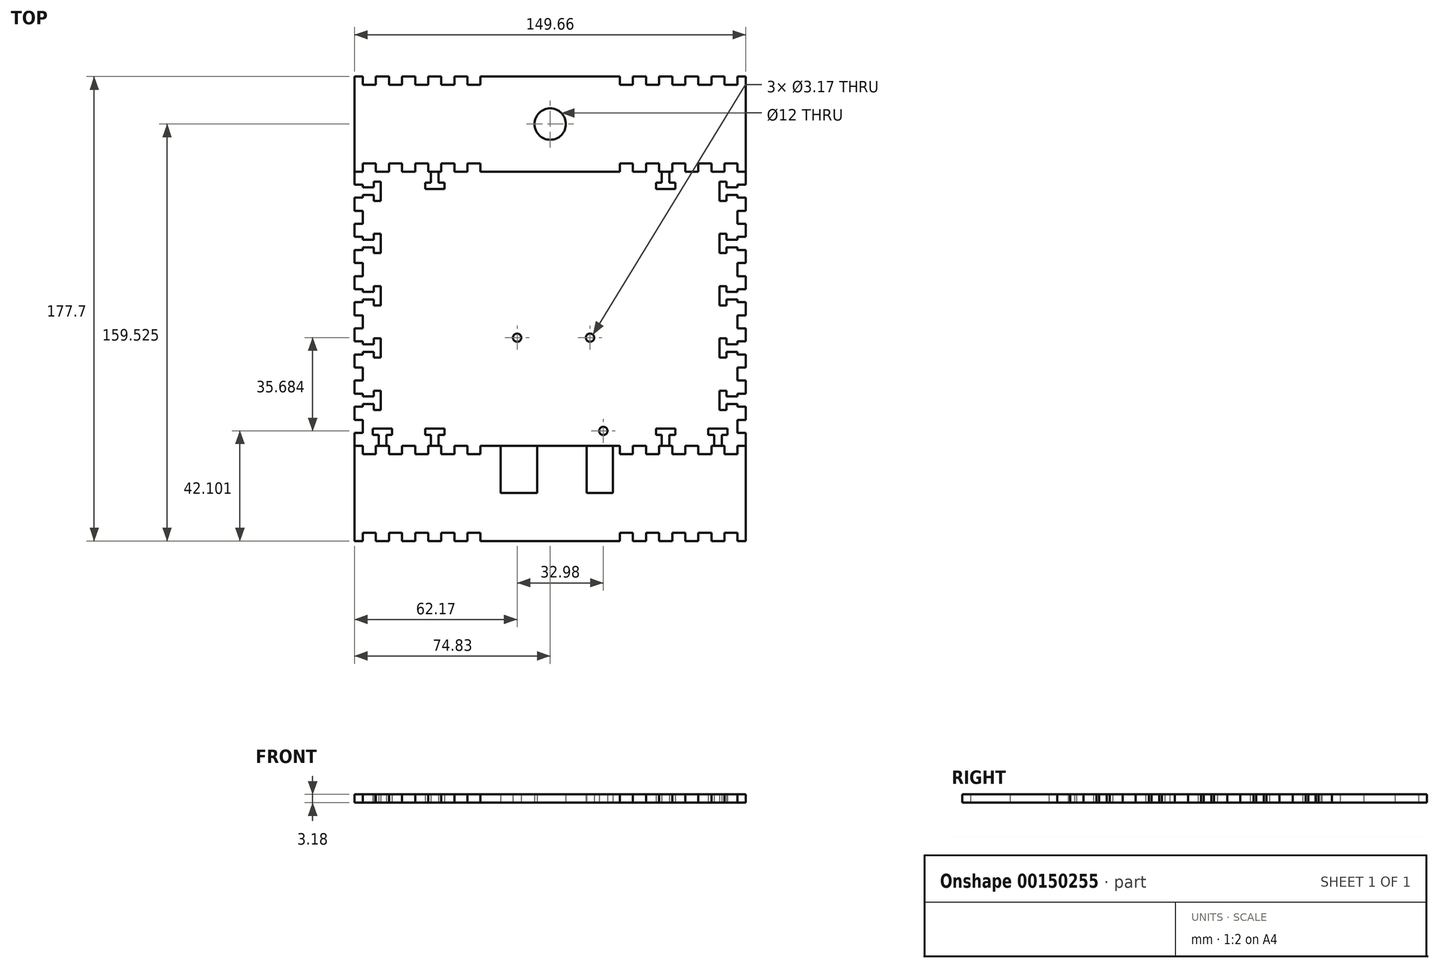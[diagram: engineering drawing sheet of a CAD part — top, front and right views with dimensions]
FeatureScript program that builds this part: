
annotation { "Feature Type Name" : "Feature", "Feature Type Description" : "" }
export const myFeature = defineFeature(function(context is Context, id is Id, definition is map)
    precondition{}
    {
        {
            var Q0;
            Q0=qCreatedBy(makeId("Top.planeOp"),FACE);
            var sketch = newSketch(context, id + "F0", { "sketchPlane" : qUnion([Q0])});
            skLineSegment(sketch, "E0", {"start": v(0, 0) * mm, "end": v(26.65, 0) * mm});
            skLineSegment(sketch, "E1", {"start": v(31.65, 0) * mm, "end": v(36.65, 0) * mm});
            skLineSegment(sketch, "E2", {"start": v(71.65, 5) * mm, "end": v(71.65, 10) * mm});
            skLineSegment(sketch, "E3", {"start": v(66.65, 105) * mm, "end": v(61.65, 105) * mm});
            skLineSegment(sketch, "E4.bottom", {"start": v(0, 105) * mm, "end": v(14.7, 105) * mm});
            skLineSegment(sketch, "E5", {"start": v(71.65, 0) * mm, "end": v(71.65, -3.17) * mm});
            skLineSegment(sketch, "E6", {"start": v(71.65, -3.17) * mm, "end": v(66.65, -3.17) * mm});
            skLineSegment(sketch, "E7", {"start": v(66.65, -3.17) * mm, "end": v(66.65, 0) * mm});
            skLineSegment(sketch, "E8.1.0.0", {"start": v(61.65, 0) * mm, "end": v(61.65, -3.17) * mm});
            skLineSegment(sketch, "E8.1.0.1", {"start": v(61.65, -3.17) * mm, "end": v(56.65, -3.17) * mm});
            skLineSegment(sketch, "E8.1.0.2", {"start": v(56.65, -3.17) * mm, "end": v(56.65, 0) * mm});
            skLineSegment(sketch, "E8.2.0.0", {"start": v(51.65, 0) * mm, "end": v(51.65, -3.17) * mm});
            skLineSegment(sketch, "E8.2.0.1", {"start": v(51.65, -3.17) * mm, "end": v(46.65, -3.17) * mm});
            skLineSegment(sketch, "E8.2.0.2", {"start": v(46.65, -3.17) * mm, "end": v(46.65, 0) * mm});
            skLineSegment(sketch, "E8.3.0.0", {"start": v(41.65, 0) * mm, "end": v(41.65, -3.17) * mm});
            skLineSegment(sketch, "E8.3.0.1", {"start": v(41.65, -3.17) * mm, "end": v(36.65, -3.17) * mm});
            skLineSegment(sketch, "E8.3.0.2", {"start": v(36.65, -3.17) * mm, "end": v(36.65, 0) * mm});
            skLineSegment(sketch, "E8.4.0.0", {"start": v(31.65, 0) * mm, "end": v(31.65, -3.17) * mm});
            skLineSegment(sketch, "E8.4.0.1", {"start": v(31.65, -3.17) * mm, "end": v(26.65, -3.17) * mm});
            skLineSegment(sketch, "E8.4.0.2", {"start": v(26.65, -3.17) * mm, "end": v(26.65, 0) * mm});
            skLineSegment(sketch, "E9", {"start": v(71.65, 0) * mm, "end": v(74.83, 0) * mm});
            skLineSegment(sketch, "E10", {"start": v(74.83, 0) * mm, "end": v(74.83, 5) * mm});
            skLineSegment(sketch, "E11", {"start": v(74.83, 5) * mm, "end": v(71.65, 5) * mm});
            skLineSegment(sketch, "E12.0.1.0", {"start": v(71.65, 10) * mm, "end": v(74.83, 10) * mm});
            skLineSegment(sketch, "E12.0.1.1", {"start": v(74.83, 10) * mm, "end": v(74.83, 15) * mm});
            skLineSegment(sketch, "E12.0.1.2", {"start": v(74.83, 15) * mm, "end": v(71.65, 15) * mm});
            skLineSegment(sketch, "E12.0.2.0", {"start": v(71.65, 20) * mm, "end": v(74.83, 20) * mm});
            skLineSegment(sketch, "E12.0.2.1", {"start": v(74.83, 20) * mm, "end": v(74.83, 25) * mm});
            skLineSegment(sketch, "E12.0.2.2", {"start": v(74.83, 25) * mm, "end": v(71.65, 25) * mm});
            skLineSegment(sketch, "E12.0.3.0", {"start": v(71.65, 30) * mm, "end": v(74.83, 30) * mm});
            skLineSegment(sketch, "E12.0.3.1", {"start": v(74.83, 30) * mm, "end": v(74.83, 35) * mm});
            skLineSegment(sketch, "E12.0.3.2", {"start": v(74.83, 35) * mm, "end": v(71.65, 35) * mm});
            skLineSegment(sketch, "E12.0.4.0", {"start": v(71.65, 40) * mm, "end": v(74.83, 40) * mm});
            skLineSegment(sketch, "E12.0.4.1", {"start": v(74.83, 40) * mm, "end": v(74.83, 45) * mm});
            skLineSegment(sketch, "E12.0.4.2", {"start": v(74.83, 45) * mm, "end": v(71.65, 45) * mm});
            skLineSegment(sketch, "E12.0.5.0", {"start": v(71.65, 50) * mm, "end": v(74.83, 50) * mm});
            skLineSegment(sketch, "E12.0.5.1", {"start": v(74.83, 50) * mm, "end": v(74.83, 55) * mm});
            skLineSegment(sketch, "E12.0.5.2", {"start": v(74.83, 55) * mm, "end": v(71.65, 55) * mm});
            skLineSegment(sketch, "E12.0.6.0", {"start": v(71.65, 60) * mm, "end": v(74.83, 60) * mm});
            skLineSegment(sketch, "E12.0.6.1", {"start": v(74.83, 60) * mm, "end": v(74.83, 65) * mm});
            skLineSegment(sketch, "E12.0.6.2", {"start": v(74.83, 65) * mm, "end": v(71.65, 65) * mm});
            skLineSegment(sketch, "E12.0.7.0", {"start": v(71.65, 70) * mm, "end": v(74.83, 70) * mm});
            skLineSegment(sketch, "E12.0.7.1", {"start": v(74.83, 70) * mm, "end": v(74.83, 75) * mm});
            skLineSegment(sketch, "E12.0.7.2", {"start": v(74.83, 75) * mm, "end": v(71.65, 75) * mm});
            skLineSegment(sketch, "E12.0.8.0", {"start": v(71.65, 80) * mm, "end": v(74.83, 80) * mm});
            skLineSegment(sketch, "E12.0.8.1", {"start": v(74.83, 80) * mm, "end": v(74.83, 85) * mm});
            skLineSegment(sketch, "E12.0.8.2", {"start": v(74.83, 85) * mm, "end": v(71.65, 85) * mm});
            skLineSegment(sketch, "E12.0.9.0", {"start": v(71.65, 90) * mm, "end": v(74.83, 90) * mm});
            skLineSegment(sketch, "E12.0.9.1", {"start": v(74.83, 90) * mm, "end": v(74.83, 95) * mm});
            skLineSegment(sketch, "E12.0.9.2", {"start": v(74.83, 95) * mm, "end": v(71.65, 95) * mm});
            skLineSegment(sketch, "E12.0.10.0", {"start": v(71.65, 100) * mm, "end": v(74.83, 100) * mm});
            skLineSegment(sketch, "E12.0.10.1", {"start": v(74.83, 100) * mm, "end": v(74.83, 105) * mm});
            skLineSegment(sketch, "E12.0.10.2", {"start": v(74.83, 105) * mm, "end": v(71.65, 105) * mm});
            skLineSegment(sketch, "E12.direction2", {"start": v(71.65, 5) * mm, "end": v(71.65, 10) * mm, "construction": true});
            skLineSegment(sketch, "E13.MirrorCS", {"start": v(26.65, 108.18) * mm, "end": v(26.65, 105) * mm});
            skLineSegment(sketch, "E14.MirrorCS", {"start": v(31.65, 108.17) * mm, "end": v(26.65, 108.17) * mm});
            skLineSegment(sketch, "E15.MirrorCS", {"start": v(31.65, 105) * mm, "end": v(31.65, 108.17) * mm});
            skLineSegment(sketch, "E16.MirrorCS", {"start": v(36.65, 108.18) * mm, "end": v(36.65, 105) * mm});
            skLineSegment(sketch, "E17.MirrorCS", {"start": v(41.65, 108.17) * mm, "end": v(36.65, 108.17) * mm});
            skLineSegment(sketch, "E18.MirrorCS", {"start": v(41.65, 105) * mm, "end": v(41.65, 108.17) * mm});
            skLineSegment(sketch, "E19.MirrorCS", {"start": v(61.65, 105) * mm, "end": v(61.65, 108.17) * mm});
            skLineSegment(sketch, "E20.MirrorCS", {"start": v(61.65, 108.17) * mm, "end": v(56.65, 108.17) * mm});
            skLineSegment(sketch, "E21.MirrorCS", {"start": v(56.65, 108.18) * mm, "end": v(56.65, 105) * mm});
            skLineSegment(sketch, "E22.MirrorCS", {"start": v(66.65, 108.18) * mm, "end": v(66.65, 105) * mm});
            skLineSegment(sketch, "E23.MirrorCS", {"start": v(71.65, 105) * mm, "end": v(71.65, 108.17) * mm});
            skLineSegment(sketch, "E24.MirrorCS", {"start": v(71.65, 108.17) * mm, "end": v(61.65, 108.17) * mm, "construction": true});
            skLineSegment(sketch, "E25.MirrorCS", {"start": v(46.65, 108.18) * mm, "end": v(46.65, 105) * mm});
            skLineSegment(sketch, "E26.MirrorCS", {"start": v(51.65, 108.17) * mm, "end": v(46.65, 108.17) * mm});
            skLineSegment(sketch, "E27.MirrorCS", {"start": v(51.65, 105) * mm, "end": v(51.65, 108.17) * mm});
            skLineSegment(sketch, "E28.MirrorCS", {"start": v(71.65, 108.17) * mm, "end": v(66.65, 108.17) * mm});
            skLineSegment(sketch, "E29.MirrorCS", {"start": v(-71.65, 105) * mm, "end": v(-71.65, 108.17) * mm});
            skLineSegment(sketch, "E30.MirrorCS", {"start": v(-31.65, 108.17) * mm, "end": v(-26.65, 108.17) * mm});
            skLineSegment(sketch, "E31.MirrorCS", {"start": v(-71.65, 108.17) * mm, "end": v(-61.65, 108.17) * mm, "construction": true});
            skLineSegment(sketch, "E32.MirrorCS", {"start": v(-26.65, 108.18) * mm, "end": v(-26.65, 105) * mm});
            skLineSegment(sketch, "E33.MirrorCS", {"start": v(-41.65, 105) * mm, "end": v(-41.65, 108.17) * mm});
            skLineSegment(sketch, "E34.MirrorCS", {"start": v(-71.65, 0) * mm, "end": v(-71.65, -3.18) * mm});
            skLineSegment(sketch, "E35.MirrorCS", {"start": v(-46.65, 108.18) * mm, "end": v(-46.65, 105) * mm});
            skLineSegment(sketch, "E36.MirrorCS", {"start": v(-36.65, 108.18) * mm, "end": v(-36.65, 105) * mm});
            skLineSegment(sketch, "E37.MirrorCS", {"start": v(-66.65, 108.17) * mm, "end": v(-66.65, 105) * mm});
            skLineSegment(sketch, "E38.MirrorCS", {"start": v(-31.65, 105) * mm, "end": v(-31.65, 108.17) * mm});
            skLineSegment(sketch, "E39.MirrorCS", {"start": v(-71.65, 108.17) * mm, "end": v(-66.65, 108.17) * mm});
            skLineSegment(sketch, "E40.MirrorCS", {"start": v(-56.65, 108.17) * mm, "end": v(-56.65, 105) * mm});
            skLineSegment(sketch, "E41.MirrorCS", {"start": v(-51.65, 105) * mm, "end": v(-51.65, 108.17) * mm});
            skLineSegment(sketch, "E42.MirrorCS", {"start": v(-61.65, 105) * mm, "end": v(-61.65, 108.17) * mm});
            skLineSegment(sketch, "E43.MirrorCS", {"start": v(-71.65, -3.18) * mm, "end": v(-66.65, -3.18) * mm});
            skLineSegment(sketch, "E44.MirrorCS", {"start": v(-74.83, 0) * mm, "end": v(-74.83, 5) * mm});
            skLineSegment(sketch, "E45.MirrorCS", {"start": v(-66.65, -3.18) * mm, "end": v(-66.65, 0) * mm});
            skLineSegment(sketch, "E46.MirrorCS", {"start": v(-74.83, 80) * mm, "end": v(-74.83, 85) * mm});
            skLineSegment(sketch, "E47.MirrorCS", {"start": v(-74.83, 105) * mm, "end": v(-71.65, 105) * mm});
            skLineSegment(sketch, "E48.MirrorCS", {"start": v(-71.65, 0) * mm, "end": v(-74.83, 0) * mm});
            skLineSegment(sketch, "E49.MirrorCS", {"start": v(-71.65, -3.18) * mm, "end": v(-61.65, -3.18) * mm, "construction": true});
            skLineSegment(sketch, "E50.MirrorCS", {"start": v(-74.83, 90) * mm, "end": v(-74.83, 95) * mm});
            skLineSegment(sketch, "E51.MirrorCS", {"start": v(-74.83, 70) * mm, "end": v(-74.83, 75) * mm});
            skLineSegment(sketch, "E52.MirrorCS", {"start": v(-74.83, 10) * mm, "end": v(-74.83, 15) * mm});
            skLineSegment(sketch, "E53.MirrorCS", {"start": v(-26.65, -3.18) * mm, "end": v(-26.65, 0) * mm});
            skLineSegment(sketch, "E54.MirrorCS", {"start": v(-71.65, 10) * mm, "end": v(-74.83, 10) * mm});
            skLineSegment(sketch, "E55.MirrorCS", {"start": v(-74.83, 60) * mm, "end": v(-74.83, 65) * mm});
            skLineSegment(sketch, "E56.MirrorCS", {"start": v(-74.83, 20) * mm, "end": v(-74.83, 25) * mm});
            skLineSegment(sketch, "E57.MirrorCS", {"start": v(-31.65, -3.18) * mm, "end": v(-26.65, -3.18) * mm});
            skLineSegment(sketch, "E58.MirrorCS", {"start": v(-74.83, 85) * mm, "end": v(-71.65, 85) * mm});
            skLineSegment(sketch, "E59.MirrorCS", {"start": v(-74.83, 55) * mm, "end": v(-71.65, 55) * mm});
            skLineSegment(sketch, "E60.MirrorCS", {"start": v(-71.65, 60) * mm, "end": v(-74.83, 60) * mm});
            skLineSegment(sketch, "E61.MirrorCS", {"start": v(-74.83, 5) * mm, "end": v(-71.65, 5) * mm});
            skLineSegment(sketch, "E62.MirrorCS", {"start": v(-41.65, 0) * mm, "end": v(-41.65, -3.18) * mm});
            skLineSegment(sketch, "E63.MirrorCS", {"start": v(-71.65, 30) * mm, "end": v(-74.83, 30) * mm});
            skLineSegment(sketch, "E64.MirrorCS", {"start": v(-51.65, 108.17) * mm, "end": v(-46.65, 108.17) * mm});
            skLineSegment(sketch, "E65.MirrorCS", {"start": v(-61.65, 108.17) * mm, "end": v(-56.65, 108.17) * mm});
            skLineSegment(sketch, "E66.MirrorCS", {"start": v(-71.65, 90) * mm, "end": v(-74.83, 90) * mm});
            skLineSegment(sketch, "E67.MirrorCS", {"start": v(-74.83, 35) * mm, "end": v(-71.65, 35) * mm});
            skLineSegment(sketch, "E68.MirrorCS", {"start": v(-36.65, -3.18) * mm, "end": v(-36.65, 0) * mm});
            skLineSegment(sketch, "E69.MirrorCS", {"start": v(-46.65, -3.18) * mm, "end": v(-46.65, 0) * mm});
            skLineSegment(sketch, "E70.MirrorCS", {"start": v(-74.83, 25) * mm, "end": v(-71.65, 25) * mm});
            skLineSegment(sketch, "E71.MirrorCS", {"start": v(-71.65, 80) * mm, "end": v(-74.83, 80) * mm});
            skLineSegment(sketch, "E72.MirrorCS", {"start": v(-71.65, 50) * mm, "end": v(-74.83, 50) * mm});
            skLineSegment(sketch, "E73.MirrorCS", {"start": v(-74.83, 45) * mm, "end": v(-71.65, 45) * mm});
            skLineSegment(sketch, "E74.MirrorCS", {"start": v(-51.65, -3.18) * mm, "end": v(-46.65, -3.18) * mm});
            skLineSegment(sketch, "E75.MirrorCS", {"start": v(-56.65, 0) * mm, "end": v(-51.65, 0) * mm});
            skLineSegment(sketch, "E76.MirrorCS", {"start": v(-74.83, 75) * mm, "end": v(-71.65, 75) * mm});
            skLineSegment(sketch, "E77.MirrorCS", {"start": v(-71.65, 100) * mm, "end": v(-74.83, 100) * mm});
            skLineSegment(sketch, "E78.MirrorCS", {"start": v(-31.65, 0) * mm, "end": v(-31.65, -3.18) * mm});
            skLineSegment(sketch, "E79.MirrorCS", {"start": v(-74.83, 15) * mm, "end": v(-71.65, 15) * mm});
            skLineSegment(sketch, "E80.MirrorCS", {"start": v(-56.65, -3.18) * mm, "end": v(-56.65, 0) * mm});
            skLineSegment(sketch, "E81.MirrorCS", {"start": v(-71.65, 40) * mm, "end": v(-74.83, 40) * mm});
            skLineSegment(sketch, "E82.MirrorCS", {"start": v(-71.65, 70) * mm, "end": v(-74.83, 70) * mm});
            skLineSegment(sketch, "E83.MirrorCS", {"start": v(-74.83, 95) * mm, "end": v(-71.65, 95) * mm});
            skLineSegment(sketch, "E84.MirrorCS", {"start": v(-61.65, -3.18) * mm, "end": v(-56.65, -3.18) * mm});
            skLineSegment(sketch, "E85.MirrorCS", {"start": v(-74.83, 65) * mm, "end": v(-71.65, 65) * mm});
            skLineSegment(sketch, "E86.MirrorCS", {"start": v(-61.65, 0) * mm, "end": v(-61.65, -3.18) * mm});
            skLineSegment(sketch, "E87.MirrorCS", {"start": v(-41.65, 108.17) * mm, "end": v(-36.65, 108.17) * mm});
            skLineSegment(sketch, "E88.MirrorCS", {"start": v(-51.65, 0) * mm, "end": v(-51.65, -3.18) * mm});
            skLineSegment(sketch, "E89.MirrorCS", {"start": v(-71.65, 20) * mm, "end": v(-74.83, 20) * mm});
            skLineSegment(sketch, "E90.MirrorCS", {"start": v(-41.65, -3.18) * mm, "end": v(-36.65, -3.18) * mm});
            skLineSegment(sketch, "E91.MirrorCS", {"start": v(-74.83, 30) * mm, "end": v(-74.83, 35) * mm});
            skLineSegment(sketch, "E92.MirrorCS", {"start": v(-71.65, 5) * mm, "end": v(-71.65, 10) * mm, "construction": true});
            skLineSegment(sketch, "E93.MirrorCS", {"start": v(-74.83, 50) * mm, "end": v(-74.83, 55) * mm});
            skLineSegment(sketch, "E94.MirrorCS", {"start": v(-74.83, 100) * mm, "end": v(-74.83, 105) * mm});
            skLineSegment(sketch, "E95.MirrorCS", {"start": v(0, 105) * mm, "end": v(-14.7, 105) * mm});
            skLineSegment(sketch, "E96.MirrorCS", {"start": v(-71.65, 5) * mm, "end": v(-71.65, 10) * mm});
            skLineSegment(sketch, "E97.MirrorCS", {"start": v(-31.65, 0) * mm, "end": v(-36.65, 0) * mm});
            skLineSegment(sketch, "E98.MirrorCS", {"start": v(-74.83, 40) * mm, "end": v(-74.83, 45) * mm});
            skLineSegment(sketch, "E99", {"start": v(-64.15, 6.6) * mm, "end": v(-62.69, 6.6) * mm});
            skLineSegment(sketch, "E100", {"start": v(-62.69, 4.2) * mm, "end": v(-62.69, 0) * mm});
            skLineSegment(sketch, "E101.MirrorCS", {"start": v(-65.61, 4.2) * mm, "end": v(-65.61, 0) * mm});
            skLineSegment(sketch, "E102.MirrorCS", {"start": v(-64.15, 6.6) * mm, "end": v(-65.61, 6.6) * mm});
            skLineSegment(sketch, "E103", {"start": v(-64.15, 6.6) * mm, "end": v(-60.47, 6.6) * mm});
            skLineSegment(sketch, "E104", {"start": v(-60.47, 6.6) * mm, "end": v(-60.47, 4.2) * mm});
            skLineSegment(sketch, "E105", {"start": v(-60.47, 4.2) * mm, "end": v(-62.69, 4.2) * mm});
            skLineSegment(sketch, "E106.MirrorCS", {"start": v(-67.83, 6.6) * mm, "end": v(-67.83, 4.2) * mm});
            skLineSegment(sketch, "E107.MirrorCS", {"start": v(-64.15, 6.6) * mm, "end": v(-67.83, 6.6) * mm});
            skLineSegment(sketch, "E108.MirrorCS", {"start": v(-67.83, 4.2) * mm, "end": v(-65.61, 4.2) * mm});
            skPoint(sketch, "E109.orphan", {"position": v(-65.61, 6.6) * mm});
            skPoint(sketch, "E110.start.orphan", {"position": v(-64.15, 0) * mm});
            skPoint(sketch, "E111.1.0.0", {"position": v(-45.61, 6.6) * mm});
            skLineSegment(sketch, "E111.1.0.1", {"start": v(-44.15, 6.6) * mm, "end": v(-47.83, 6.6) * mm});
            skLineSegment(sketch, "E111.1.0.2", {"start": v(-45.61, 4.2) * mm, "end": v(-45.61, 0) * mm});
            skLineSegment(sketch, "E111.1.0.3", {"start": v(-47.83, 4.2) * mm, "end": v(-45.61, 4.2) * mm});
            skLineSegment(sketch, "E111.1.0.4", {"start": v(-44.15, 6.6) * mm, "end": v(-40.47, 6.6) * mm});
            skLineSegment(sketch, "E111.1.0.5", {"start": v(-40.47, 6.6) * mm, "end": v(-40.47, 4.2) * mm});
            skLineSegment(sketch, "E111.1.0.6", {"start": v(-40.47, 4.2) * mm, "end": v(-42.69, 4.2) * mm});
            skLineSegment(sketch, "E111.1.0.7", {"start": v(-47.83, 6.6) * mm, "end": v(-47.83, 4.2) * mm});
            skLineSegment(sketch, "E111.1.0.8", {"start": v(-42.69, 4.2) * mm, "end": v(-42.69, 0) * mm});
            skLineSegment(sketch, "E111.1.0.9", {"start": v(-44.15, 6.6) * mm, "end": v(-45.61, 6.6) * mm});
            skLineSegment(sketch, "E111.1.0.10", {"start": v(-44.15, 6.6) * mm, "end": v(-42.69, 6.6) * mm});
            skLineSegment(sketch, "E111.direction1", {"start": v(-62.69, 0) * mm, "end": v(-61.65, 0) * mm, "construction": true});
            skLineSegment(sketch, "E112", {"start": v(-71.65, 18.96) * mm, "end": v(-67.46, 18.96) * mm});
            skLineSegment(sketch, "E113", {"start": v(-67.46, 18.96) * mm, "end": v(-67.46, 21.18) * mm});
            skLineSegment(sketch, "E114", {"start": v(-67.46, 21.18) * mm, "end": v(-64.79, 21.18) * mm});
            skLineSegment(sketch, "E115", {"start": v(-64.79, 21.18) * mm, "end": v(-64.79, 13.82) * mm});
            skLineSegment(sketch, "E116", {"start": v(-64.79, 13.82) * mm, "end": v(-67.46, 13.82) * mm});
            skLineSegment(sketch, "E117", {"start": v(-67.46, 13.82) * mm, "end": v(-67.46, 16.04) * mm});
            skLineSegment(sketch, "E118", {"start": v(-67.46, 16.04) * mm, "end": v(-71.65, 16.04) * mm});
            skLineSegment(sketch, "E119.0.1.0", {"start": v(-67.46, 36.04) * mm, "end": v(-71.65, 36.04) * mm});
            skLineSegment(sketch, "E119.0.1.1", {"start": v(-67.46, 33.82) * mm, "end": v(-67.46, 36.04) * mm});
            skLineSegment(sketch, "E119.0.1.2", {"start": v(-64.79, 33.82) * mm, "end": v(-67.46, 33.82) * mm});
            skLineSegment(sketch, "E119.0.1.3", {"start": v(-67.46, 41.18) * mm, "end": v(-64.79, 41.18) * mm});
            skLineSegment(sketch, "E119.0.1.4", {"start": v(-64.79, 41.18) * mm, "end": v(-64.79, 33.82) * mm});
            skLineSegment(sketch, "E119.0.1.5", {"start": v(-67.46, 38.96) * mm, "end": v(-67.46, 41.18) * mm});
            skLineSegment(sketch, "E119.0.1.6", {"start": v(-71.65, 38.96) * mm, "end": v(-67.46, 38.96) * mm});
            skLineSegment(sketch, "E119.0.2.0", {"start": v(-67.46, 56.04) * mm, "end": v(-71.65, 56.04) * mm});
            skLineSegment(sketch, "E119.0.2.1", {"start": v(-67.46, 53.82) * mm, "end": v(-67.46, 56.04) * mm});
            skLineSegment(sketch, "E119.0.2.2", {"start": v(-64.79, 53.82) * mm, "end": v(-67.46, 53.82) * mm});
            skLineSegment(sketch, "E119.0.2.3", {"start": v(-67.46, 61.18) * mm, "end": v(-64.79, 61.18) * mm});
            skLineSegment(sketch, "E119.0.2.4", {"start": v(-64.79, 61.18) * mm, "end": v(-64.79, 53.82) * mm});
            skLineSegment(sketch, "E119.0.2.5", {"start": v(-67.46, 58.96) * mm, "end": v(-67.46, 61.18) * mm});
            skLineSegment(sketch, "E119.0.2.6", {"start": v(-71.65, 58.96) * mm, "end": v(-67.46, 58.96) * mm});
            skLineSegment(sketch, "E119.0.3.0", {"start": v(-67.46, 76.04) * mm, "end": v(-71.65, 76.04) * mm});
            skLineSegment(sketch, "E119.0.3.1", {"start": v(-67.46, 73.82) * mm, "end": v(-67.46, 76.04) * mm});
            skLineSegment(sketch, "E119.0.3.2", {"start": v(-64.79, 73.82) * mm, "end": v(-67.46, 73.82) * mm});
            skLineSegment(sketch, "E119.0.3.3", {"start": v(-67.46, 81.18) * mm, "end": v(-64.79, 81.18) * mm});
            skLineSegment(sketch, "E119.0.3.4", {"start": v(-64.79, 81.18) * mm, "end": v(-64.79, 73.82) * mm});
            skLineSegment(sketch, "E119.0.3.5", {"start": v(-67.46, 78.96) * mm, "end": v(-67.46, 81.18) * mm});
            skLineSegment(sketch, "E119.0.3.6", {"start": v(-71.65, 78.96) * mm, "end": v(-67.46, 78.96) * mm});
            skLineSegment(sketch, "E119.0.4.0", {"start": v(-67.46, 96.04) * mm, "end": v(-71.65, 96.04) * mm});
            skLineSegment(sketch, "E119.0.4.1", {"start": v(-67.46, 93.82) * mm, "end": v(-67.46, 96.04) * mm});
            skLineSegment(sketch, "E119.0.4.2", {"start": v(-64.79, 93.82) * mm, "end": v(-67.46, 93.82) * mm});
            skLineSegment(sketch, "E119.0.4.3", {"start": v(-67.46, 101.18) * mm, "end": v(-64.79, 101.18) * mm});
            skLineSegment(sketch, "E119.0.4.4", {"start": v(-64.79, 101.18) * mm, "end": v(-64.79, 93.82) * mm});
            skLineSegment(sketch, "E119.0.4.5", {"start": v(-67.46, 98.96) * mm, "end": v(-67.46, 101.18) * mm});
            skLineSegment(sketch, "E119.0.4.6", {"start": v(-71.65, 98.96) * mm, "end": v(-67.46, 98.96) * mm});
            skLineSegment(sketch, "E119.direction1", {"start": v(-71.65, 16.04) * mm, "end": v(-46.65, 16.04) * mm, "construction": true});
            skLineSegment(sketch, "E119.direction2", {"start": v(-71.65, 18.96) * mm, "end": v(-71.65, 20) * mm, "construction": true});
            skLineSegment(sketch, "E120.trimOffspring", {"start": v(-45.61, 0) * mm, "end": v(-46.65, 0) * mm});
            skLineSegment(sketch, "E121.trimOffspring", {"start": v(-71.65, 38.96) * mm, "end": v(-71.65, 40) * mm});
            skLineSegment(sketch, "E122.trimOffspring", {"start": v(-71.65, 78.96) * mm, "end": v(-71.65, 80) * mm});
            skLineSegment(sketch, "E123.trimOffspring", {"start": v(-71.65, 98.96) * mm, "end": v(-71.65, 100) * mm});
            skLineSegment(sketch, "E124.trimOffspring", {"start": v(-71.65, 58.96) * mm, "end": v(-71.65, 60) * mm});
            skLineSegment(sketch, "E125", {"start": v(-71.65, 36.04) * mm, "end": v(-71.65, 35) * mm});
            skLineSegment(sketch, "E126.trimOffspring", {"start": v(-65.61, 0) * mm, "end": v(-66.65, 0) * mm});
            skLineSegment(sketch, "E127.trimOffspring", {"start": v(-71.65, 18.96) * mm, "end": v(-71.65, 20) * mm});
            skPoint(sketch, "E128.orphan", {"position": v(-71.65, 105) * mm});
            skLineSegment(sketch, "E129.trimOffspring", {"start": v(-56.65, 105) * mm, "end": v(-51.65, 105) * mm});
            skLineSegment(sketch, "E130.trimOffspring", {"start": v(-36.65, 105) * mm, "end": v(-31.65, 105) * mm});
            skLineSegment(sketch, "E131", {"start": v(-66.65, 105) * mm, "end": v(-61.65, 105) * mm});
            skLineSegment(sketch, "E132", {"start": v(-46.65, 105) * mm, "end": v(-45.61, 105) * mm});
            skLineSegment(sketch, "E133.trimOffspring", {"start": v(-26.65, 105) * mm, "end": v(0, 105) * mm});
            skLineSegment(sketch, "E134.trimOffspring", {"start": v(26.65, 105) * mm, "end": v(0, 105) * mm});
            skLineSegment(sketch, "E135.trimOffspring", {"start": v(36.65, 105) * mm, "end": v(31.65, 105) * mm});
            skLineSegment(sketch, "E136.trimOffspring", {"start": v(46.65, 105) * mm, "end": v(45.61, 105) * mm});
            skLineSegment(sketch, "E137.trimOffspring", {"start": v(56.65, 105) * mm, "end": v(51.65, 105) * mm});
            skPoint(sketch, "E138.orphan", {"position": v(71.65, 105) * mm});
            skLineSegment(sketch, "E139.trimOffspring", {"start": v(71.65, 95) * mm, "end": v(71.65, 96.04) * mm});
            skLineSegment(sketch, "E140.trimOffspring", {"start": v(71.65, 85) * mm, "end": v(71.65, 90) * mm});
            skLineSegment(sketch, "E141.trimOffspring", {"start": v(71.65, 75) * mm, "end": v(71.65, 76.04) * mm});
            skLineSegment(sketch, "E142.trimOffspring", {"start": v(71.65, 65) * mm, "end": v(71.65, 70) * mm});
            skLineSegment(sketch, "E143.trimOffspring", {"start": v(71.65, 55) * mm, "end": v(71.65, 56.04) * mm});
            skLineSegment(sketch, "E144.trimOffspring", {"start": v(71.65, 45) * mm, "end": v(71.65, 50) * mm});
            skLineSegment(sketch, "E145.trimOffspring", {"start": v(71.65, 35) * mm, "end": v(71.65, 36.04) * mm});
            skLineSegment(sketch, "E146.trimOffspring", {"start": v(71.65, 25) * mm, "end": v(71.65, 30) * mm});
            skLineSegment(sketch, "E147.trimOffspring", {"start": v(71.65, 15) * mm, "end": v(71.65, 16.04) * mm});
            skLineSegment(sketch, "E148.trimOffspring", {"start": v(61.65, 0) * mm, "end": v(62.69, 0) * mm});
            skLineSegment(sketch, "E149.trimOffspring", {"start": v(51.65, 0) * mm, "end": v(56.65, 0) * mm});
            skLineSegment(sketch, "E150.trimOffspring", {"start": v(41.65, 0) * mm, "end": v(42.69, 0) * mm});
            skLineSegment(sketch, "E151.trimOffspring", {"start": v(-41.65, 0) * mm, "end": v(-42.69, 0) * mm});
            skLineSegment(sketch, "E152.trimOffspring", {"start": v(-46.65, 0) * mm, "end": v(-45.61, 0) * mm, "construction": true});
            skLineSegment(sketch, "E153.trimOffspring", {"start": v(-56.65, 0) * mm, "end": v(-51.65, 0) * mm, "construction": true});
            skLineSegment(sketch, "E154.trimOffspring", {"start": v(-61.65, 0) * mm, "end": v(-62.69, 0) * mm});
            skLineSegment(sketch, "E155.trimOffspring", {"start": v(-51.65, 0) * mm, "end": v(-56.65, 0) * mm});
            skLineSegment(sketch, "E156.trimOffspring", {"start": v(-71.65, 95) * mm, "end": v(-71.65, 96.04) * mm});
            skLineSegment(sketch, "E157.trimOffspring", {"start": v(-71.65, 85) * mm, "end": v(-71.65, 90) * mm});
            skLineSegment(sketch, "E158.trimOffspring", {"start": v(-71.65, 75) * mm, "end": v(-71.65, 76.04) * mm});
            skLineSegment(sketch, "E159.trimOffspring", {"start": v(-71.65, 65) * mm, "end": v(-71.65, 70) * mm});
            skLineSegment(sketch, "E160.trimOffspring", {"start": v(-71.65, 55) * mm, "end": v(-71.65, 56.04) * mm});
            skLineSegment(sketch, "E161.trimOffspring", {"start": v(-71.65, 45) * mm, "end": v(-71.65, 50) * mm});
            skLineSegment(sketch, "E162.trimOffspring", {"start": v(-71.65, 35) * mm, "end": v(-71.65, 36.04) * mm, "construction": true});
            skLineSegment(sketch, "E163.trimOffspring", {"start": v(-71.65, 25) * mm, "end": v(-71.65, 30) * mm, "construction": true});
            skLineSegment(sketch, "E164.trimOffspring", {"start": v(-71.65, 25) * mm, "end": v(-71.65, 30) * mm});
            skLineSegment(sketch, "E165.trimOffspring", {"start": v(-71.65, 15) * mm, "end": v(-71.65, 16.04) * mm});
            skLineSegment(sketch, "E166.MirrorCS", {"start": v(-44.15, 98.4) * mm, "end": v(-45.61, 98.4) * mm});
            skLineSegment(sketch, "E167.MirrorCS", {"start": v(-44.15, 98.4) * mm, "end": v(-47.83, 98.4) * mm});
            skLineSegment(sketch, "E168.MirrorCS", {"start": v(-44.15, 98.4) * mm, "end": v(-42.69, 98.4) * mm});
            skLineSegment(sketch, "E169.MirrorCS", {"start": v(-40.47, 98.4) * mm, "end": v(-40.47, 100.8) * mm});
            skLineSegment(sketch, "E170.MirrorCS", {"start": v(-44.15, 98.4) * mm, "end": v(-40.47, 98.4) * mm});
            skLineSegment(sketch, "E171.MirrorCS", {"start": v(-47.83, 100.8) * mm, "end": v(-45.61, 100.8) * mm});
            skLineSegment(sketch, "E172.MirrorCS", {"start": v(-45.61, 100.8) * mm, "end": v(-45.61, 105) * mm});
            skPoint(sketch, "E173.MirrorP", {"position": v(-45.61, 98.4) * mm});
            skLineSegment(sketch, "E174.MirrorCS", {"start": v(-42.69, 100.8) * mm, "end": v(-42.69, 105) * mm});
            skLineSegment(sketch, "E175.MirrorCS", {"start": v(-47.83, 98.4) * mm, "end": v(-47.83, 100.8) * mm});
            skLineSegment(sketch, "E176.MirrorCS", {"start": v(-40.47, 100.8) * mm, "end": v(-42.69, 100.8) * mm});
            skLineSegment(sketch, "E177.MirrorCS", {"start": v(64.15, 6.6) * mm, "end": v(65.61, 6.6) * mm});
            skLineSegment(sketch, "E178.MirrorCS", {"start": v(44.15, 6.6) * mm, "end": v(45.61, 6.6) * mm});
            skLineSegment(sketch, "E179.MirrorCS", {"start": v(44.15, 6.6) * mm, "end": v(42.69, 6.6) * mm});
            skLineSegment(sketch, "E180.MirrorCS", {"start": v(44.15, 6.6) * mm, "end": v(47.83, 6.6) * mm});
            skLineSegment(sketch, "E181.MirrorCS", {"start": v(64.15, 6.6) * mm, "end": v(62.69, 6.6) * mm});
            skLineSegment(sketch, "E182.MirrorCS", {"start": v(65.61, 4.2) * mm, "end": v(65.61, 0) * mm});
            skLineSegment(sketch, "E183.MirrorCS", {"start": v(64.15, 6.6) * mm, "end": v(60.47, 6.6) * mm});
            skLineSegment(sketch, "E184.MirrorCS", {"start": v(60.47, 6.6) * mm, "end": v(60.47, 4.2) * mm});
            skPoint(sketch, "E185.MirrorP", {"position": v(65.61, 6.6) * mm});
            skLineSegment(sketch, "E186.MirrorCS", {"start": v(60.47, 4.2) * mm, "end": v(62.69, 4.2) * mm});
            skLineSegment(sketch, "E187.MirrorCS", {"start": v(67.83, 4.2) * mm, "end": v(65.61, 4.2) * mm});
            skLineSegment(sketch, "E188.MirrorCS", {"start": v(67.83, 6.6) * mm, "end": v(67.83, 4.2) * mm});
            skPoint(sketch, "E189.MirrorP", {"position": v(45.61, 6.6) * mm});
            skLineSegment(sketch, "E190.MirrorCS", {"start": v(64.15, 6.6) * mm, "end": v(67.83, 6.6) * mm});
            skLineSegment(sketch, "E191.MirrorCS", {"start": v(45.61, 4.2) * mm, "end": v(45.61, 0) * mm});
            skLineSegment(sketch, "E192.MirrorCS", {"start": v(47.83, 4.2) * mm, "end": v(45.61, 4.2) * mm});
            skLineSegment(sketch, "E193.MirrorCS", {"start": v(44.15, 6.6) * mm, "end": v(40.47, 6.6) * mm});
            skLineSegment(sketch, "E194.MirrorCS", {"start": v(40.47, 6.6) * mm, "end": v(40.47, 4.2) * mm});
            skLineSegment(sketch, "E195.MirrorCS", {"start": v(40.47, 4.2) * mm, "end": v(42.69, 4.2) * mm});
            skLineSegment(sketch, "E196.MirrorCS", {"start": v(47.83, 6.6) * mm, "end": v(47.83, 4.2) * mm});
            skLineSegment(sketch, "E197.MirrorCS", {"start": v(62.69, 4.2) * mm, "end": v(62.69, 0) * mm});
            skLineSegment(sketch, "E198.MirrorCS", {"start": v(42.69, 4.2) * mm, "end": v(42.69, 0) * mm});
            skLineSegment(sketch, "E199.MirrorCS", {"start": v(64.79, 33.82) * mm, "end": v(67.46, 33.82) * mm});
            skLineSegment(sketch, "E200.MirrorCS", {"start": v(67.46, 33.82) * mm, "end": v(67.46, 36.04) * mm});
            skLineSegment(sketch, "E201.MirrorCS", {"start": v(67.46, 81.18) * mm, "end": v(64.79, 81.18) * mm});
            skLineSegment(sketch, "E202.MirrorCS", {"start": v(64.79, 73.82) * mm, "end": v(67.46, 73.82) * mm});
            skLineSegment(sketch, "E203.MirrorCS", {"start": v(67.46, 58.96) * mm, "end": v(67.46, 61.18) * mm});
            skLineSegment(sketch, "E204.MirrorCS", {"start": v(67.46, 16.04) * mm, "end": v(71.65, 16.04) * mm});
            skLineSegment(sketch, "E205.MirrorCS", {"start": v(67.46, 73.82) * mm, "end": v(67.46, 76.04) * mm});
            skLineSegment(sketch, "E206.MirrorCS", {"start": v(67.46, 13.82) * mm, "end": v(67.46, 16.04) * mm});
            skLineSegment(sketch, "E207.MirrorCS", {"start": v(67.46, 21.18) * mm, "end": v(64.79, 21.18) * mm});
            skLineSegment(sketch, "E208.MirrorCS", {"start": v(64.79, 13.82) * mm, "end": v(67.46, 13.82) * mm});
            skLineSegment(sketch, "E209.MirrorCS", {"start": v(67.46, 98.96) * mm, "end": v(67.46, 101.18) * mm});
            skLineSegment(sketch, "E210.MirrorCS", {"start": v(67.46, 61.18) * mm, "end": v(64.79, 61.18) * mm});
            skLineSegment(sketch, "E211.MirrorCS", {"start": v(67.46, 18.96) * mm, "end": v(67.46, 21.18) * mm});
            skLineSegment(sketch, "E212.MirrorCS", {"start": v(64.79, 53.82) * mm, "end": v(67.46, 53.82) * mm});
            skLineSegment(sketch, "E213.MirrorCS", {"start": v(67.46, 101.18) * mm, "end": v(64.79, 101.18) * mm});
            skLineSegment(sketch, "E214.MirrorCS", {"start": v(67.46, 53.82) * mm, "end": v(67.46, 56.04) * mm});
            skLineSegment(sketch, "E215.MirrorCS", {"start": v(64.79, 93.82) * mm, "end": v(67.46, 93.82) * mm});
            skLineSegment(sketch, "E216.MirrorCS", {"start": v(67.46, 93.82) * mm, "end": v(67.46, 96.04) * mm});
            skLineSegment(sketch, "E217.MirrorCS", {"start": v(67.46, 38.96) * mm, "end": v(67.46, 41.18) * mm});
            skLineSegment(sketch, "E218.MirrorCS", {"start": v(67.46, 41.18) * mm, "end": v(64.79, 41.18) * mm});
            skLineSegment(sketch, "E219.MirrorCS", {"start": v(67.46, 78.96) * mm, "end": v(67.46, 81.18) * mm});
            skLineSegment(sketch, "E220.MirrorCS", {"start": v(71.65, 16.04) * mm, "end": v(46.65, 16.04) * mm, "construction": true});
            skLineSegment(sketch, "E221.MirrorCS", {"start": v(71.65, 18.96) * mm, "end": v(67.46, 18.96) * mm});
            skLineSegment(sketch, "E222.MirrorCS", {"start": v(64.79, 81.18) * mm, "end": v(64.79, 73.82) * mm});
            skLineSegment(sketch, "E223.MirrorCS", {"start": v(67.46, 36.04) * mm, "end": v(71.65, 36.04) * mm});
            skLineSegment(sketch, "E224.MirrorCS", {"start": v(64.79, 21.18) * mm, "end": v(64.79, 13.82) * mm});
            skLineSegment(sketch, "E225.MirrorCS", {"start": v(67.46, 76.04) * mm, "end": v(71.65, 76.04) * mm});
            skLineSegment(sketch, "E226.MirrorCS", {"start": v(71.65, 98.96) * mm, "end": v(67.46, 98.96) * mm});
            skLineSegment(sketch, "E227.MirrorCS", {"start": v(64.79, 61.18) * mm, "end": v(64.79, 53.82) * mm});
            skLineSegment(sketch, "E228.MirrorCS", {"start": v(71.65, 58.96) * mm, "end": v(67.46, 58.96) * mm});
            skLineSegment(sketch, "E229.MirrorCS", {"start": v(64.79, 101.18) * mm, "end": v(64.79, 93.82) * mm});
            skLineSegment(sketch, "E230.MirrorCS", {"start": v(67.46, 56.04) * mm, "end": v(71.65, 56.04) * mm});
            skLineSegment(sketch, "E231.MirrorCS", {"start": v(71.65, 38.96) * mm, "end": v(67.46, 38.96) * mm});
            skLineSegment(sketch, "E232.MirrorCS", {"start": v(67.46, 96.04) * mm, "end": v(71.65, 96.04) * mm});
            skLineSegment(sketch, "E233.MirrorCS", {"start": v(64.79, 41.18) * mm, "end": v(64.79, 33.82) * mm});
            skLineSegment(sketch, "E234.MirrorCS", {"start": v(71.65, 78.96) * mm, "end": v(67.46, 78.96) * mm});
            skLineSegment(sketch, "E235.MirrorCS", {"start": v(44.15, 98.4) * mm, "end": v(45.61, 98.4) * mm});
            skLineSegment(sketch, "E236.MirrorCS", {"start": v(47.83, 98.4) * mm, "end": v(47.83, 100.8) * mm});
            skLineSegment(sketch, "E237.MirrorCS", {"start": v(42.69, 100.8) * mm, "end": v(42.69, 105) * mm});
            skLineSegment(sketch, "E238.MirrorCS", {"start": v(45.61, 100.8) * mm, "end": v(45.61, 105) * mm});
            skLineSegment(sketch, "E239.MirrorCS", {"start": v(44.15, 98.4) * mm, "end": v(42.69, 98.4) * mm});
            skLineSegment(sketch, "E240.MirrorCS", {"start": v(47.83, 100.8) * mm, "end": v(45.61, 100.8) * mm});
            skLineSegment(sketch, "E241.MirrorCS", {"start": v(44.15, 98.4) * mm, "end": v(40.47, 98.4) * mm});
            skLineSegment(sketch, "E242.MirrorCS", {"start": v(44.15, 98.4) * mm, "end": v(47.83, 98.4) * mm});
            skLineSegment(sketch, "E243.MirrorCS", {"start": v(40.47, 98.4) * mm, "end": v(40.47, 100.8) * mm});
            skPoint(sketch, "E244.MirrorP", {"position": v(45.61, 98.4) * mm});
            skLineSegment(sketch, "E245.MirrorCS", {"start": v(40.47, 100.8) * mm, "end": v(42.69, 100.8) * mm});
            skLineSegment(sketch, "E246.trimOffspring", {"start": v(42.69, 105) * mm, "end": v(41.65, 105) * mm});
            skLineSegment(sketch, "E247.trimOffspring", {"start": v(-42.69, 105) * mm, "end": v(-41.65, 105) * mm});
            skLineSegment(sketch, "E248.trimOffspring", {"start": v(71.65, 98.96) * mm, "end": v(71.65, 100) * mm});
            skLineSegment(sketch, "E249.trimOffspring", {"start": v(71.65, 78.96) * mm, "end": v(71.65, 80) * mm});
            skLineSegment(sketch, "E250.trimOffspring", {"start": v(71.65, 58.96) * mm, "end": v(71.65, 60) * mm});
            skLineSegment(sketch, "E251.trimOffspring", {"start": v(71.65, 38.96) * mm, "end": v(71.65, 40) * mm});
            skLineSegment(sketch, "E252.trimOffspring", {"start": v(71.65, 18.96) * mm, "end": v(71.65, 20) * mm});
            skLineSegment(sketch, "E253.trimOffspring", {"start": v(65.61, 0) * mm, "end": v(66.65, 0) * mm});
            skLineSegment(sketch, "E254.trimOffspring", {"start": v(45.61, 0) * mm, "end": v(46.65, 0) * mm});
            skLineSegment(sketch, "E255", {"start": v(71.65, 98.96) * mm, "end": v(71.65, 96.04) * mm});
            skLineSegment(sketch, "E256", {"start": v(71.65, 78.96) * mm, "end": v(71.65, 76.04) * mm});
            skLineSegment(sketch, "E257", {"start": v(71.65, 58.96) * mm, "end": v(71.65, 56.04) * mm});
            skLineSegment(sketch, "E258", {"start": v(71.65, 38.96) * mm, "end": v(71.65, 36.04) * mm});
            skLineSegment(sketch, "E259", {"start": v(71.65, 18.96) * mm, "end": v(71.65, 16.04) * mm});
            skCircle(sketch, "E260", {"center": v(73.24, 97.5) * mm, "radius": 1.59 * mm});
            skPoint(sketch, "E260.centerSnap0", {"position": v(71.65, 97.5) * mm});
            skPoint(sketch, "E260.centerSnap1", {"position": v(73.24, 100) * mm});
            skCircle(sketch, "E261.0.1.0", {"center": v(73.24, 77.5) * mm, "radius": 1.59 * mm});
            skCircle(sketch, "E261.0.2.0", {"center": v(73.24, 57.5) * mm, "radius": 1.59 * mm});
            skCircle(sketch, "E261.0.3.0", {"center": v(73.24, 37.5) * mm, "radius": 1.59 * mm});
            skCircle(sketch, "E261.0.4.0", {"center": v(73.24, 17.5) * mm, "radius": 1.59 * mm});
            skLineSegment(sketch, "E261.direction2", {"start": v(73.24, 97.5) * mm, "end": v(73.24, 77.5) * mm, "construction": true});
            skCircle(sketch, "E262.MirrorC", {"center": v(-73.24, 97.5) * mm, "radius": 1.59 * mm});
            skLineSegment(sketch, "E263.MirrorCS", {"start": v(-71.65, 98.96) * mm, "end": v(-71.65, 96.04) * mm});
            skLineSegment(sketch, "E264.MirrorCS", {"start": v(-71.65, 78.96) * mm, "end": v(-71.65, 76.04) * mm});
            skCircle(sketch, "E265.MirrorC", {"center": v(-73.24, 57.5) * mm, "radius": 1.59 * mm});
            skLineSegment(sketch, "E266.MirrorCS", {"start": v(-71.65, 58.96) * mm, "end": v(-71.65, 56.04) * mm});
            skLineSegment(sketch, "E267.MirrorCS", {"start": v(-71.65, 35) * mm, "end": v(-71.65, 36.04) * mm});
            skLineSegment(sketch, "E268.MirrorCS", {"start": v(-71.65, 38.96) * mm, "end": v(-71.65, 36.04) * mm});
            skCircle(sketch, "E269.MirrorC", {"center": v(-73.24, 77.5) * mm, "radius": 1.59 * mm});
            skCircle(sketch, "E270.MirrorC", {"center": v(-73.24, 37.5) * mm, "radius": 1.59 * mm});
            skCircle(sketch, "E271.MirrorC", {"center": v(-73.24, 17.5) * mm, "radius": 1.59 * mm});
            skLineSegment(sketch, "E272.MirrorCS", {"start": v(-71.65, 18.96) * mm, "end": v(-71.65, 16.04) * mm});
            skLineSegment(sketch, "E273", {"start": v(-74.83, 105) * mm, "end": v(-74.83, 138.17) * mm});
            skLineSegment(sketch, "E274", {"start": v(-74.83, 138.17) * mm, "end": v(-74.83, 108.17) * mm});
            skLineSegment(sketch, "E275.MirrorCS", {"start": v(-74.83, 141.35) * mm, "end": v(-71.65, 141.35) * mm});
            skLineSegment(sketch, "E276.MirrorCS", {"start": v(-71.65, 141.35) * mm, "end": v(-71.65, 138.17) * mm});
            skLineSegment(sketch, "E277.MirrorCS", {"start": v(-66.65, 138.17) * mm, "end": v(-66.65, 141.35) * mm});
            skLineSegment(sketch, "E278.MirrorCS", {"start": v(-74.83, 141.35) * mm, "end": v(-74.83, 108.17) * mm});
            skLineSegment(sketch, "E279.MirrorCS", {"start": v(-61.65, 138.17) * mm, "end": v(-56.65, 138.17) * mm});
            skLineSegment(sketch, "E280.MirrorCS", {"start": v(-56.65, 138.17) * mm, "end": v(-56.65, 141.35) * mm});
            skLineSegment(sketch, "E281.MirrorCS", {"start": v(-56.65, 141.35) * mm, "end": v(-51.65, 141.35) * mm});
            skLineSegment(sketch, "E282.MirrorCS", {"start": v(-51.65, 141.35) * mm, "end": v(-51.65, 138.17) * mm});
            skLineSegment(sketch, "E283.MirrorCS", {"start": v(-51.65, 138.17) * mm, "end": v(-46.65, 138.17) * mm});
            skLineSegment(sketch, "E284.MirrorCS", {"start": v(-46.65, 138.17) * mm, "end": v(-46.65, 141.35) * mm});
            skLineSegment(sketch, "E285.MirrorCS", {"start": v(-41.65, 141.35) * mm, "end": v(-41.65, 138.17) * mm});
            skLineSegment(sketch, "E286.MirrorCS", {"start": v(-41.65, 138.17) * mm, "end": v(-36.65, 138.17) * mm});
            skLineSegment(sketch, "E287.MirrorCS", {"start": v(-36.65, 138.17) * mm, "end": v(-36.65, 141.35) * mm});
            skLineSegment(sketch, "E288.MirrorCS", {"start": v(-36.65, 141.35) * mm, "end": v(-31.65, 141.35) * mm});
            skLineSegment(sketch, "E289.MirrorCS", {"start": v(-31.65, 141.35) * mm, "end": v(-31.65, 138.17) * mm});
            skLineSegment(sketch, "E290.MirrorCS", {"start": v(-31.65, 138.17) * mm, "end": v(-26.65, 138.17) * mm});
            skLineSegment(sketch, "E291.MirrorCS", {"start": v(-26.65, 138.17) * mm, "end": v(-26.65, 141.35) * mm});
            skLineSegment(sketch, "E292.MirrorCS", {"start": v(-26.65, 141.35) * mm, "end": v(0, 141.35) * mm});
            skLineSegment(sketch, "E293", {"start": v(-71.65, 138.17) * mm, "end": v(-66.65, 138.17) * mm});
            skLineSegment(sketch, "E294", {"start": v(-66.65, 141.35) * mm, "end": v(-61.65, 141.35) * mm});
            skLineSegment(sketch, "E295", {"start": v(-61.65, 141.35) * mm, "end": v(-61.65, 138.17) * mm});
            skLineSegment(sketch, "E296", {"start": v(-46.65, 141.35) * mm, "end": v(-41.65, 141.35) * mm});
            skLineSegment(sketch, "E297.MirrorCS", {"start": v(41.65, 138.17) * mm, "end": v(36.65, 138.17) * mm});
            skLineSegment(sketch, "E298.MirrorCS", {"start": v(66.65, 141.35) * mm, "end": v(61.65, 141.35) * mm});
            skLineSegment(sketch, "E299.MirrorCS", {"start": v(56.65, 138.17) * mm, "end": v(56.65, 141.35) * mm});
            skLineSegment(sketch, "E300.MirrorCS", {"start": v(61.65, 141.35) * mm, "end": v(61.65, 138.17) * mm});
            skLineSegment(sketch, "E301.MirrorCS", {"start": v(56.65, 141.35) * mm, "end": v(51.65, 141.35) * mm});
            skLineSegment(sketch, "E302.MirrorCS", {"start": v(51.65, 141.35) * mm, "end": v(51.65, 138.17) * mm});
            skLineSegment(sketch, "E303.MirrorCS", {"start": v(46.65, 138.17) * mm, "end": v(46.65, 141.35) * mm});
            skLineSegment(sketch, "E304.MirrorCS", {"start": v(41.65, 141.35) * mm, "end": v(41.65, 138.17) * mm});
            skLineSegment(sketch, "E305.MirrorCS", {"start": v(36.65, 138.17) * mm, "end": v(36.65, 141.35) * mm});
            skLineSegment(sketch, "E306.MirrorCS", {"start": v(74.83, 105) * mm, "end": v(74.83, 138.17) * mm});
            skLineSegment(sketch, "E307.MirrorCS", {"start": v(31.65, 141.35) * mm, "end": v(31.65, 138.17) * mm});
            skLineSegment(sketch, "E308.MirrorCS", {"start": v(26.65, 138.17) * mm, "end": v(26.65, 141.35) * mm});
            skLineSegment(sketch, "E309.MirrorCS", {"start": v(74.83, 141.35) * mm, "end": v(71.65, 141.35) * mm});
            skLineSegment(sketch, "E310.MirrorCS", {"start": v(71.65, 141.35) * mm, "end": v(71.65, 138.17) * mm});
            skLineSegment(sketch, "E311.MirrorCS", {"start": v(66.65, 138.17) * mm, "end": v(66.65, 141.35) * mm});
            skLineSegment(sketch, "E312.MirrorCS", {"start": v(74.83, 138.17) * mm, "end": v(74.83, 108.17) * mm});
            skLineSegment(sketch, "E313.MirrorCS", {"start": v(61.65, 138.17) * mm, "end": v(56.65, 138.17) * mm});
            skLineSegment(sketch, "E314.MirrorCS", {"start": v(46.65, 141.35) * mm, "end": v(41.65, 141.35) * mm});
            skLineSegment(sketch, "E315.MirrorCS", {"start": v(51.65, 138.17) * mm, "end": v(46.65, 138.17) * mm});
            skLineSegment(sketch, "E316.MirrorCS", {"start": v(36.65, 141.35) * mm, "end": v(31.65, 141.35) * mm});
            skLineSegment(sketch, "E317.MirrorCS", {"start": v(31.65, 138.17) * mm, "end": v(26.65, 138.17) * mm});
            skLineSegment(sketch, "E318.MirrorCS", {"start": v(26.65, 141.35) * mm, "end": v(0, 141.35) * mm});
            skLineSegment(sketch, "E319.MirrorCS", {"start": v(71.65, 138.17) * mm, "end": v(66.65, 138.17) * mm});
            skLineSegment(sketch, "E320.MirrorCS", {"start": v(74.83, 141.35) * mm, "end": v(74.83, 108.17) * mm});
            skLineSegment(sketch, "E321.MirrorCS", {"start": v(-41.65, -33.17) * mm, "end": v(-36.65, -33.17) * mm});
            skLineSegment(sketch, "E322.MirrorCS", {"start": v(41.65, -33.17) * mm, "end": v(36.65, -33.17) * mm});
            skLineSegment(sketch, "E323.MirrorCS", {"start": v(36.65, -33.17) * mm, "end": v(36.65, -36.35) * mm});
            skLineSegment(sketch, "E324.MirrorCS", {"start": v(41.65, -36.35) * mm, "end": v(41.65, -33.18) * mm});
            skLineSegment(sketch, "E325.MirrorCS", {"start": v(-41.65, -36.35) * mm, "end": v(-41.65, -33.18) * mm});
            skLineSegment(sketch, "E326.MirrorCS", {"start": v(-36.65, -33.17) * mm, "end": v(-36.65, -36.35) * mm});
            skLineSegment(sketch, "E327.MirrorCS", {"start": v(-31.65, -36.35) * mm, "end": v(-31.65, -33.18) * mm});
            skLineSegment(sketch, "E328.MirrorCS", {"start": v(-74.83, 0) * mm, "end": v(-74.83, -33.18) * mm});
            skLineSegment(sketch, "E329.MirrorCS", {"start": v(71.65, -33.18) * mm, "end": v(66.65, -33.17) * mm});
            skLineSegment(sketch, "E330.MirrorCS", {"start": v(46.65, -33.17) * mm, "end": v(46.65, -36.35) * mm});
            skLineSegment(sketch, "E331.MirrorCS", {"start": v(-31.65, -33.17) * mm, "end": v(-26.65, -33.17) * mm});
            skLineSegment(sketch, "E332.MirrorCS", {"start": v(-26.65, -33.17) * mm, "end": v(-26.65, -36.35) * mm});
            skLineSegment(sketch, "E333.MirrorCS", {"start": v(-74.83, -36.35) * mm, "end": v(-71.65, -36.35) * mm});
            skLineSegment(sketch, "E334.MirrorCS", {"start": v(-71.65, -36.35) * mm, "end": v(-71.65, -33.18) * mm});
            skLineSegment(sketch, "E335.MirrorCS", {"start": v(-66.65, -33.17) * mm, "end": v(-66.65, -36.35) * mm});
            skLineSegment(sketch, "E336.MirrorCS", {"start": v(31.65, -36.35) * mm, "end": v(31.65, -33.18) * mm});
            skLineSegment(sketch, "E337.MirrorCS", {"start": v(-71.65, -33.18) * mm, "end": v(-66.65, -33.17) * mm});
            skLineSegment(sketch, "E338.MirrorCS", {"start": v(26.65, -33.17) * mm, "end": v(26.65, -36.35) * mm});
            skLineSegment(sketch, "E339.MirrorCS", {"start": v(-66.65, -36.35) * mm, "end": v(-61.65, -36.35) * mm});
            skLineSegment(sketch, "E340.MirrorCS", {"start": v(-61.65, -33.18) * mm, "end": v(-56.65, -33.18) * mm});
            skLineSegment(sketch, "E341.MirrorCS", {"start": v(74.83, -36.35) * mm, "end": v(71.65, -36.35) * mm});
            skLineSegment(sketch, "E342.MirrorCS", {"start": v(-61.65, -36.35) * mm, "end": v(-61.65, -33.18) * mm});
            skLineSegment(sketch, "E343.MirrorCS", {"start": v(-56.65, -33.17) * mm, "end": v(-56.65, -36.35) * mm});
            skLineSegment(sketch, "E344.MirrorCS", {"start": v(71.65, -36.35) * mm, "end": v(71.65, -33.18) * mm});
            skLineSegment(sketch, "E345.MirrorCS", {"start": v(-46.65, -36.35) * mm, "end": v(-41.65, -36.35) * mm});
            skLineSegment(sketch, "E346.MirrorCS", {"start": v(-56.65, -36.35) * mm, "end": v(-51.65, -36.35) * mm});
            skLineSegment(sketch, "E347.MirrorCS", {"start": v(66.65, -33.17) * mm, "end": v(66.65, -36.35) * mm});
            skLineSegment(sketch, "E348.MirrorCS", {"start": v(-51.65, -36.35) * mm, "end": v(-51.65, -33.18) * mm});
            skLineSegment(sketch, "E349.MirrorCS", {"start": v(61.65, -33.18) * mm, "end": v(56.65, -33.18) * mm});
            skLineSegment(sketch, "E350.MirrorCS", {"start": v(-51.65, -33.17) * mm, "end": v(-46.65, -33.17) * mm});
            skLineSegment(sketch, "E351.MirrorCS", {"start": v(74.83, -36.35) * mm, "end": v(74.83, -3.17) * mm});
            skLineSegment(sketch, "E352.MirrorCS", {"start": v(66.65, -36.35) * mm, "end": v(61.65, -36.35) * mm});
            skLineSegment(sketch, "E353.MirrorCS", {"start": v(46.65, -36.35) * mm, "end": v(41.65, -36.35) * mm});
            skLineSegment(sketch, "E354.MirrorCS", {"start": v(-46.65, -33.17) * mm, "end": v(-46.65, -36.35) * mm});
            skLineSegment(sketch, "E355.MirrorCS", {"start": v(56.65, -33.17) * mm, "end": v(56.65, -36.35) * mm});
            skLineSegment(sketch, "E356.MirrorCS", {"start": v(51.65, -33.17) * mm, "end": v(46.65, -33.17) * mm});
            skLineSegment(sketch, "E357.MirrorCS", {"start": v(36.65, -36.35) * mm, "end": v(31.65, -36.35) * mm});
            skLineSegment(sketch, "E358.MirrorCS", {"start": v(61.65, -36.35) * mm, "end": v(61.65, -33.18) * mm});
            skLineSegment(sketch, "E359.MirrorCS", {"start": v(31.65, -33.17) * mm, "end": v(26.65, -33.17) * mm});
            skLineSegment(sketch, "E360.MirrorCS", {"start": v(56.65, -36.35) * mm, "end": v(51.65, -36.35) * mm});
            skLineSegment(sketch, "E361.MirrorCS", {"start": v(51.65, -36.35) * mm, "end": v(51.65, -33.18) * mm});
            skLineSegment(sketch, "E362.MirrorCS", {"start": v(-36.65, -36.35) * mm, "end": v(-31.65, -36.35) * mm});
            skLineSegment(sketch, "E363.MirrorCS", {"start": v(-74.83, -33.18) * mm, "end": v(-74.83, -3.17) * mm});
            skLineSegment(sketch, "E364.MirrorCS", {"start": v(74.83, 0) * mm, "end": v(74.83, -33.18) * mm});
            skLineSegment(sketch, "E365.MirrorCS", {"start": v(-26.65, -36.35) * mm, "end": v(0, -36.35) * mm});
            skLineSegment(sketch, "E366.MirrorCS", {"start": v(-74.83, -36.35) * mm, "end": v(-74.83, -3.17) * mm});
            skLineSegment(sketch, "E367.MirrorCS", {"start": v(74.83, -33.18) * mm, "end": v(74.83, -3.17) * mm});
            skLineSegment(sketch, "E368.MirrorCS", {"start": v(26.65, -36.35) * mm, "end": v(0, -36.35) * mm});
            skCircle(sketch, "E369", {"center": v(20.32, 5.75) * mm, "radius": 1.59 * mm});
            skCircle(sketch, "E370", {"center": v(15.24, 41.44) * mm, "radius": 1.59 * mm});
            skCircle(sketch, "E371", {"center": v(-12.66, 41.44) * mm, "radius": 1.59 * mm});
            skCircle(sketch, "E372", {"center": v(0, 123.17) * mm, "radius": 6 * mm});
            skLineSegment(sketch, "E373", {"start": v(0, 0) * mm, "end": v(-26.65, 0) * mm});
            skLineSegment(sketch, "E374.MirrorCS", {"start": v(-18.94, 0) * mm, "end": v(-18.94, -18) * mm});
            skLineSegment(sketch, "E375.MirrorCS", {"start": v(-18.94, -18) * mm, "end": v(-4.94, -18) * mm});
            skLineSegment(sketch, "E376.MirrorCS", {"start": v(-4.94, -18) * mm, "end": v(-4.94, 0) * mm});
            skLineSegment(sketch, "E377", {"start": v(23.94, 0) * mm, "end": v(23.94, -18) * mm});
            skLineSegment(sketch, "E378", {"start": v(23.94, -18) * mm, "end": v(13.94, -18) * mm});
            skLineSegment(sketch, "E379", {"start": v(13.94, -18) * mm, "end": v(13.94, 0) * mm});
            skPoint(sketch, "E380.orphan", {"position": v(27.94, 0) * mm});
            skLineSegment(sketch, "E381.trimOffspring", {"start": v(-46.65, 0) * mm, "end": v(-42.69, 0) * mm});
            skLineSegment(sketch, "E382.trimOffspring", {"start": v(-36.65, 0) * mm, "end": v(-31.65, 0) * mm});
            skLineSegment(sketch, "E383", {"start": v(-45.61, 105) * mm, "end": v(-41.65, 105) * mm});
            skLineSegment(sketch, "E384", {"start": v(42.69, 105) * mm, "end": v(45.61, 105) * mm});
            skLineSegment(sketch, "E385", {"start": v(62.69, 0) * mm, "end": v(65.61, 0) * mm});
            skLineSegment(sketch, "E386", {"start": v(42.69, 0) * mm, "end": v(45.61, 0) * mm});
            skLineSegment(sketch, "E387", {"start": v(-65.61, 0) * mm, "end": v(-62.69, 0) * mm});
            skSolve(sketch);
        }
        {
            var Q0;
            Q0=makeQuery(id+"F0.imprint","IMPRINT",FACE,{"disambiguationData":[TD([[makeQuery(id+"F0.imprint","IMPRINT",EDGE,{"derivedFrom":sQuery(id+"F0.wireOp",EDGE,"E1")}),1.0]])]});
            extrude(context, id + "F1", {"entities" : qUnion([Q0]), "depth" : 3.17 * mm});
        }
        {
            var Q0;
            Q0=makeQuery(id+"F0.imprint","IMPRINT",FACE,{"disambiguationData":[TD([[makeQuery(id+"F0.imprint","IMPRINT",EDGE,{"derivedFrom":sQuery(id+"F0.wireOp",EDGE,"E3")}),-1.0]])]});
            extrude(context, id + "F2", {"entities" : qUnion([Q0]), "depth" : 3.17 * mm});
        }
        {
            var Q0;
            Q0=makeQuery(id+"F0.imprint","IMPRINT",FACE,{"disambiguationData":[TD([[makeQuery(id+"F0.imprint","IMPRINT",EDGE,{"derivedFrom":sQuery(id+"F0.wireOp",EDGE,"E1")}),-1.0]])]});
            extrude(context, id + "F3", {"entities" : qUnion([Q0]), "depth" : 3.17 * mm});
        }
    });
